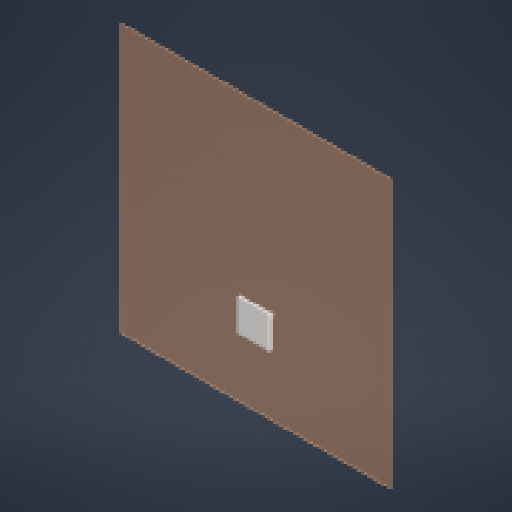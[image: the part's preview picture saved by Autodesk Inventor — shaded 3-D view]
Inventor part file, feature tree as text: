
AUTODESK INVENTOR PART (.ipt)
format: ipt  version: 2023.1 (Build 271208000, 208)  size: 194,560 bytes
history: native  units: mm
features: other x3, plane x2, extrude x2, sketch x2, pattern_linear x1
ambient origin geometry x8: Origin, YZ Plane, XZ Plane, XY Plane, X Axis, Y Axis, Z Axis, Center Point
bodies: Solid1 (feature_tree)
feature tree (10):
  plane  "Work Plane1"
  plane  "Work Plane2"
  extrude  "Extrusion1"  Depth=38.9mm
  extrude  "Extrusion2"  Depth=3.0mm TaperAngle=0.0deg
  pattern_linear  "Rectangular Pattern1"  Spacing1=5.0mm  [1 undecoded]
  sketch  "Sketch1"  dims[d3=70.0mm d4=38.9mm]
  sketch  "Sketch2"  dims[d5=38.9mm d6=3.0mm d7=0.0mm d8=5.0mm d9=5.0mm d10=3.0mm d11=0.0mm d12=50.0mm d14=7.5mm d15=50.0mm d17=7.5mm d18=2.0mm d19=2.0mm]
  parser-record x1  (decoder bookkeeping rows leaked as tree rows — omitted from the tree; the rows remain in map.json)
  other  "Beau4tClock.iam"
  other  "Clock:1"
note: 1 required parameter value undecoded (feature->parameter linkage not recoverable at this tier; creation-order binding heuristic only, values carry confidence <= 0.55)
note: 1 file-system path scrubbed to <path> (originals preserved in map.json)
